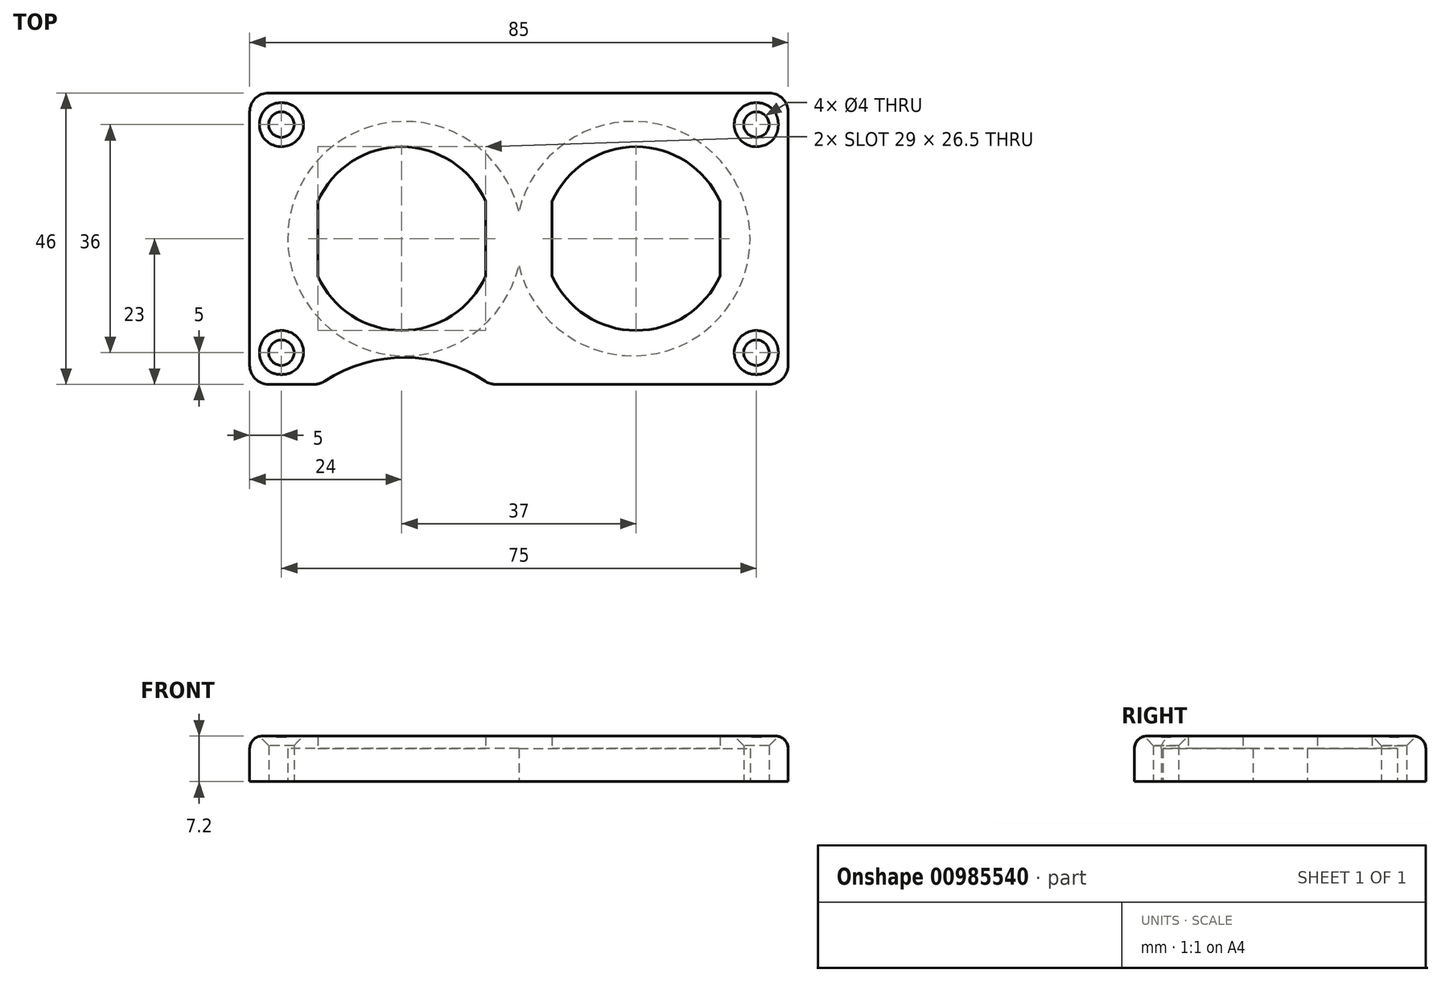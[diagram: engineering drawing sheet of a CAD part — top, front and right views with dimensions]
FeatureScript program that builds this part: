
annotation { "Feature Type Name" : "Feature", "Feature Type Description" : "" }
export const myFeature = defineFeature(function(context is Context, id is Id, definition is map)
    precondition{}
    {
        {
            var Q0;
            Q0=qCreatedBy(makeId("Top.planeOp"),FACE);
            var sketch = newSketch(context, id + "F0", { "sketchPlane" : qUnion([Q0])});
            skLineSegment(sketch, "E0", {"start": v(39.5, -23) * mm, "end": v(-3.68, -23) * mm});
            skLineSegment(sketch, "E1", {"start": v(42.5, 23) * mm, "end": v(-42.5, 23) * mm});
            skPoint(sketch, "E2.orphan", {"position": v(0, 23) * mm});
            skPoint(sketch, "E3.orphan", {"position": v(-42.5, 0) * mm});
            skPoint(sketch, "E4.orphan", {"position": v(42.5, 0) * mm});
            skArc(sketch, "E5", {"start": v(5.25, -5.89) * mm, "mid": v(18.5, -14.5) * mm, "end": v(31.75, -5.89) * mm});
            skArc(sketch, "E6.1.0.0", {"start": v(-5.25, 5.89) * mm, "mid": v(-18.5, 14.5) * mm, "end": v(-31.75, 5.89) * mm});
            skLineSegment(sketch, "E6.direction1", {"start": v(18.5, 0) * mm, "end": v(-18.5, 0) * mm, "construction": true});
            skLineSegment(sketch, "E7.trimOffspring", {"start": v(-32.32, -23) * mm, "end": v(-39.5, -23) * mm});
            skLineSegment(sketch, "E8", {"start": v(42.5, -20) * mm, "end": v(42.5, 20) * mm});
            skLineSegment(sketch, "E9", {"start": v(-39.5, 23) * mm, "end": v(39.5, 23) * mm});
            skLineSegment(sketch, "E10", {"start": v(-33, 0) * mm, "end": v(-43, 0) * mm});
            skLineSegment(sketch, "E11", {"start": v(-42.5, -20) * mm, "end": v(-42.5, 20) * mm});
            skCircle(sketch, "E12", {"center": v(37.5, 18) * mm, "radius": 2 * mm});
            skCircle(sketch, "E13.0.1.0", {"center": v(37.5, -18) * mm, "radius": 2 * mm});
            skCircle(sketch, "E13.1.0.0", {"center": v(-37.5, 18) * mm, "radius": 2 * mm});
            skCircle(sketch, "E13.1.1.0", {"center": v(-37.5, -18) * mm, "radius": 2 * mm});
            skLineSegment(sketch, "E13.direction1", {"start": v(37.5, 18) * mm, "end": v(-37.5, 18) * mm, "construction": true});
            skLineSegment(sketch, "E13.direction2", {"start": v(37.5, 18) * mm, "end": v(37.5, -18) * mm, "construction": true});
            skPoint(sketch, "E14.visualSharp", {"position": v(-42.5, 23) * mm});
            skArc(sketch, "E14.filletArc", {"start": v(-39.5, 23) * mm, "mid": v(-41.62, 22.12) * mm, "end": v(-42.5, 20) * mm});
            skPoint(sketch, "E15.visualSharp", {"position": v(42.5, 23) * mm});
            skArc(sketch, "E15.filletArc", {"start": v(42.5, 20) * mm, "mid": v(41.62, 22.12) * mm, "end": v(39.5, 23) * mm});
            skPoint(sketch, "E16.visualSharp", {"position": v(42.5, -23) * mm});
            skArc(sketch, "E16.filletArc", {"start": v(39.5, -23) * mm, "mid": v(41.62, -22.12) * mm, "end": v(42.5, -20) * mm});
            skPoint(sketch, "E17.visualSharp", {"position": v(-42.5, -23) * mm});
            skArc(sketch, "E17.filletArc", {"start": v(-42.5, -20) * mm, "mid": v(-41.62, -22.12) * mm, "end": v(-39.5, -23) * mm});
            skLineSegment(sketch, "E18", {"start": v(-31.75, -5.89) * mm, "end": v(-31.75, 5.89) * mm});
            skLineSegment(sketch, "E19", {"start": v(-5.25, -5.89) * mm, "end": v(-5.25, 5.89) * mm});
            skLineSegment(sketch, "E20", {"start": v(5.25, -5.89) * mm, "end": v(5.25, 5.89) * mm});
            skLineSegment(sketch, "E21", {"start": v(31.75, -5.89) * mm, "end": v(31.75, 5.89) * mm});
            skPoint(sketch, "E22.orphan", {"position": v(-31.75, 0) * mm});
            skPoint(sketch, "E23.orphan", {"position": v(31.75, 0) * mm});
            skArc(sketch, "E24.trimOffspring", {"start": v(31.75, 5.89) * mm, "mid": v(18.5, 14.5) * mm, "end": v(5.25, 5.89) * mm});
            skArc(sketch, "E25.trimOffspring", {"start": v(-31.75, -5.89) * mm, "mid": v(-18.5, -14.5) * mm, "end": v(-5.25, -5.89) * mm});
            skArc(sketch, "E26", {"start": v(-5.32, -22.51) * mm, "mid": v(-18, -18.75) * mm, "end": v(-30.68, -22.51) * mm});
            skPoint(sketch, "E27.visualSharp", {"position": v(-31.4, -23) * mm});
            skArc(sketch, "E27.filletArc", {"start": v(-32.32, -23) * mm, "mid": v(-31.47, -22.88) * mm, "end": v(-30.68, -22.51) * mm});
            skPoint(sketch, "E28.visualSharp", {"position": v(-4.6, -23) * mm});
            skArc(sketch, "E28.filletArc", {"start": v(-5.32, -22.51) * mm, "mid": v(-4.53, -22.88) * mm, "end": v(-3.68, -23) * mm});
            skSolve(sketch);
        }
        {
            var Q0;
            Q0 = qSketchRegion(id + "F0", true);
            extrude(context, id + "F1", {"entities" : qUnion([Q0]), "depth" : 7.2 * mm, "offsetDistance" : 25 * mm});
        }
        {
            var Q0;
            Q0=makeQuery(id+"F1.opExtrude","CAP_FACE",FACE,{"disambiguationData":[OSD([sQuery(id+"F0.wireOp",EDGE,"E0"),sQuery(id+"F0.wireOp",EDGE,"E5"),sQuery(id+"F0.wireOp",EDGE,"E6.1.0.0"),sQuery(id+"F0.wireOp",EDGE,"bJdMWulF-XVvQ-XwlP-b5f5-Oh9jKwaFxzj5"),sQuery(id+"F0.wireOp",EDGE,"E7.trimOffspring"),sQuery(id+"F0.wireOp",EDGE,"E8"),sQuery(id+"F0.wireOp",EDGE,"E9"),sQuery(id+"F0.wireOp",EDGE,"E11"),sQuery(id+"F0.wireOp",EDGE,"E12"),sQuery(id+"F0.wireOp",EDGE,"E13.0.1.0"),sQuery(id+"F0.wireOp",EDGE,"E13.1.0.0"),sQuery(id+"F0.wireOp",EDGE,"E13.1.1.0"),sQuery(id+"F0.wireOp",EDGE,"E14.filletArc"),sQuery(id+"F0.wireOp",EDGE,"E15.filletArc"),sQuery(id+"F0.wireOp",EDGE,"E16.filletArc"),sQuery(id+"F0.wireOp",EDGE,"E17.filletArc"),sQuery(id+"F0.wireOp",EDGE,"47bbfd85-ed48-445f-85e0-7e442efd98a2.filletArc"),sQuery(id+"F0.wireOp",EDGE,"76a7e08d-4759-4fa9-b712-5606076e1a33.filletArc")])],"isStart":true});
            var sketch = newSketch(context, id + "F2", { "sketchPlane" : qUnion([Q0])});
            skArc(sketch, "E29", {"start": v(0, -4.27) * mm, "mid": v(36.5, 0) * mm, "end": v(0, 4.27) * mm});
            skArc(sketch, "E30", {"start": v(0, 4.27) * mm, "mid": v(-36.5, 0) * mm, "end": v(0, -4.27) * mm});
            skSolve(sketch);
        }
        {
            var Q0;
            Q0 = qSketchRegion(id + "F2", true);
            extrude(context, id + "F3", {"entities" : qUnion([Q0]), "operationType" : NewBodyOperationType.REMOVE, "oppositeDirection" : true, "depth" : 5.2 * mm, "offsetDistance" : 25 * mm});
        }
        {
            var Q0;
            Q0=makeQuery(id+"F1.opExtrude","CAP_EDGE",EDGE,{"disambiguationData":[OSD([sQuery(id+"F0.wireOp",EDGE,"E9")])],"isStart":false});
            var Q1;
            Q1=makeQuery(id+"F1.opExtrude","CAP_EDGE",EDGE,{"disambiguationData":[OSD([sQuery(id+"F0.wireOp",EDGE,"E14.filletArc")])],"isStart":false});
            var Q2;
            Q2=makeQuery(id+"F1.opExtrude","CAP_EDGE",EDGE,{"disambiguationData":[OSD([sQuery(id+"F0.wireOp",EDGE,"E11")])],"isStart":false});
            var Q3;
            Q3=makeQuery(id+"F1.opExtrude","CAP_EDGE",EDGE,{"disambiguationData":[OSD([sQuery(id+"F0.wireOp",EDGE,"E17.filletArc")])],"isStart":false});
            var Q4;
            Q4=makeQuery(id+"F1.opExtrude","CAP_EDGE",EDGE,{"disambiguationData":[OSD([sQuery(id+"F0.wireOp",EDGE,"E7.trimOffspring")])],"isStart":false});
            var Q5;
            Q5=makeQuery(id+"F1.opExtrude","CAP_EDGE",EDGE,{"disambiguationData":[OSD([sQuery(id+"F0.wireOp",EDGE,"47bbfd85-ed48-445f-85e0-7e442efd98a2.filletArc")])],"isStart":false});
            var Q6;
            Q6=makeQuery(id+"F1.opExtrude","CAP_EDGE",EDGE,{"disambiguationData":[OSD([sQuery(id+"F0.wireOp",EDGE,"bJdMWulF-XVvQ-XwlP-b5f5-Oh9jKwaFxzj5")])],"isStart":false});
            var Q7;
            Q7=makeQuery(id+"F1.opExtrude","CAP_EDGE",EDGE,{"disambiguationData":[OSD([sQuery(id+"F0.wireOp",EDGE,"76a7e08d-4759-4fa9-b712-5606076e1a33.filletArc")])],"isStart":false});
            var Q8;
            Q8=makeQuery(id+"F1.opExtrude","CAP_EDGE",EDGE,{"disambiguationData":[OSD([sQuery(id+"F0.wireOp",EDGE,"E0")])],"isStart":false});
            var Q9;
            Q9=makeQuery(id+"F1.opExtrude","CAP_EDGE",EDGE,{"disambiguationData":[OSD([sQuery(id+"F0.wireOp",EDGE,"E16.filletArc")])],"isStart":false});
            var Q10;
            Q10=makeQuery(id+"F1.opExtrude","CAP_EDGE",EDGE,{"disambiguationData":[OSD([sQuery(id+"F0.wireOp",EDGE,"E8")])],"isStart":false});
            var Q11;
            Q11=makeQuery(id+"F1.opExtrude","CAP_EDGE",EDGE,{"disambiguationData":[OSD([sQuery(id+"F0.wireOp",EDGE,"E15.filletArc")])],"isStart":false});
            fillet(context, id + "F4", {"entities" : qUnion([Q0, Q1, Q2, Q3, Q4, Q5, Q6, Q7, Q8, Q9, Q10, Q11]), "radius" : 2 * mm, "tangentPropagation" : true, "allowEdgeOverflow" : false});
        }
        {
            var Q0;
            Q0=makeQuery(id+"F1.opExtrude","CAP_EDGE",EDGE,{"disambiguationData":[OSD([sQuery(id+"F0.wireOp",EDGE,"E13.1.0.0")])],"isStart":false});
            var Q1;
            Q1=makeQuery(id+"F1.opExtrude","CAP_EDGE",EDGE,{"disambiguationData":[OSD([sQuery(id+"F0.wireOp",EDGE,"E13.1.1.0")])],"isStart":false});
            var Q2;
            Q2=makeQuery(id+"F1.opExtrude","CAP_EDGE",EDGE,{"disambiguationData":[OSD([sQuery(id+"F0.wireOp",EDGE,"E13.0.1.0")])],"isStart":false});
            var Q3;
            Q3=makeQuery(id+"F1.opExtrude","CAP_EDGE",EDGE,{"disambiguationData":[OSD([sQuery(id+"F0.wireOp",EDGE,"E12")])],"isStart":false});
            chamfer(context, id + "F5", {"entities" : qUnion([Q0, Q1, Q2, Q3]), "width" : 1.5 * mm, "tangentPropagation" : true});
        }
    });
